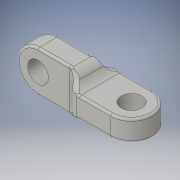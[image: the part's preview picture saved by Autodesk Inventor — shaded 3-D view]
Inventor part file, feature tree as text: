
AUTODESK INVENTOR PART (.ipt)
format: ipt  version: 2016 (Build 200138000, 138)  size: 240,128 bytes
history: native  units: in
note: dims shown in document units (in); Inventor stores cm internally (conversion verified against a paired STEP export)
features: extrude x4, fillet x4, sketch x4
ambient origin geometry x8: Origin, YZ Plane, XZ Plane, XY Plane, X Axis, Y Axis, Z Axis, Center Point
bodies: Solid1 (feature_tree)
feature tree (12):
  extrude  "Extrusion1"  Depth=0.75in
  extrude  "Extrusion2"  Depth=0.25in
  fillet  "Fillet1"  Radius=0.125in
  fillet  "Fillet2"  Radius=0.25in
  fillet  "Fillet3"  Radius=0.125in
  sketch  "Sketch3"  dims[d8=0.75in d9=0.0in d10=0.25in]
  extrude  "Extrusion3"  Depth=0.25in
  extrude  "Extrusion4"  Depth=0.025in
  fillet  "Fillet4"  Radius=0.25in
  sketch  "Sketch1"  dims[d0=0.5in d1=0.75in]
  sketch  "Sketch2"  dims[d2=0.25in d3=0.0in d4=0.5in d5=0.125in d6=0.25in d7=0.125in]
  sketch  "Sketch4"  dims[d11=0.125in d12=0.125in d13=0.25in d14=0.25in d15=0.75in d16=0.0in d17=0.75in d18=0.0in d19=0.025in]
